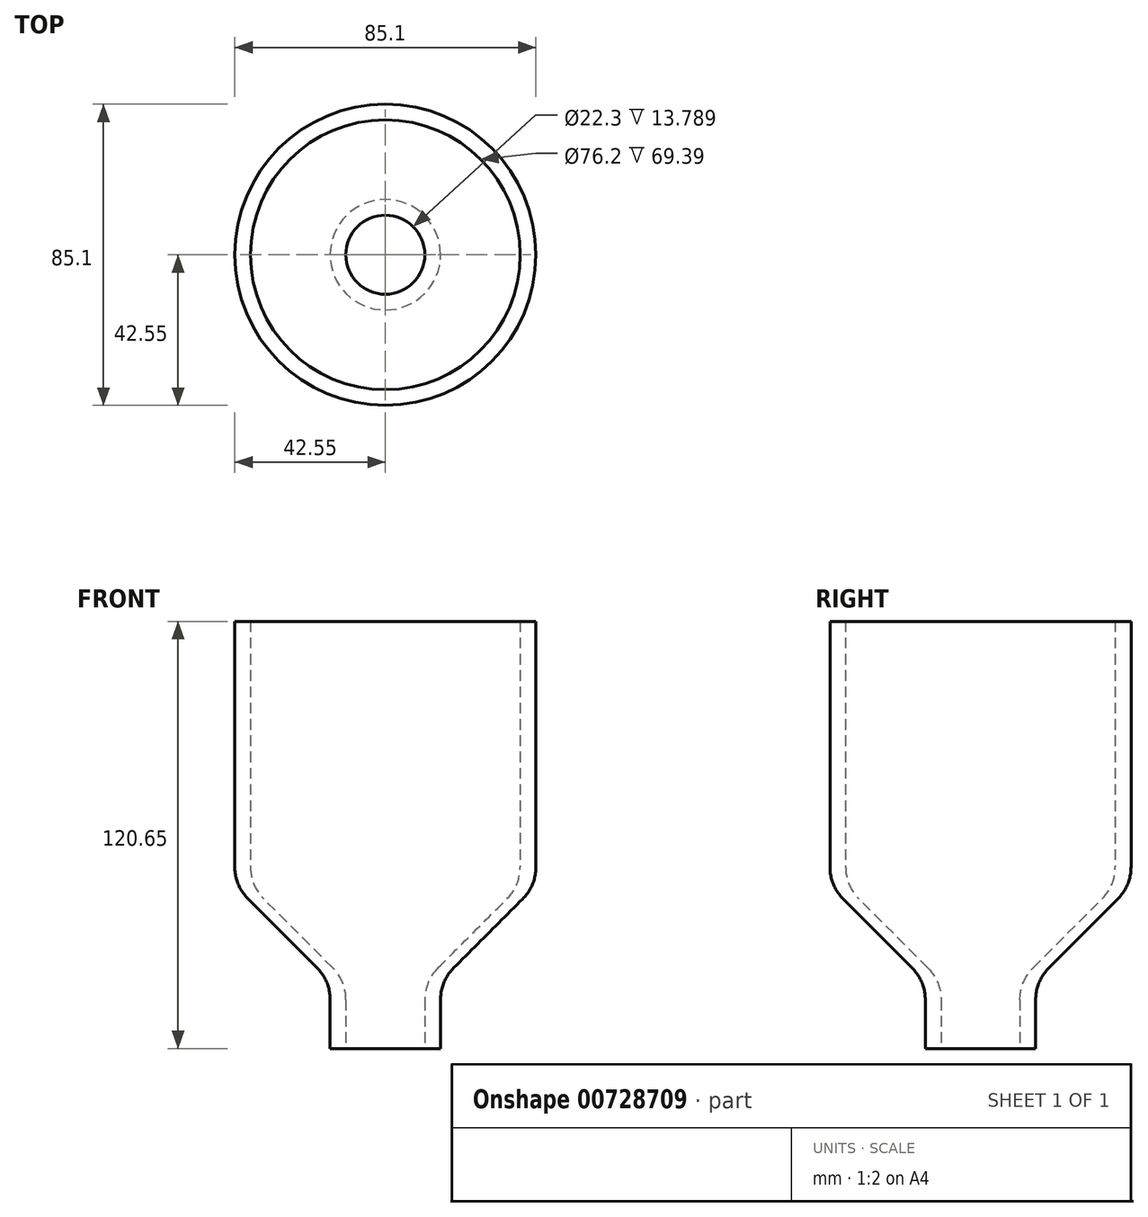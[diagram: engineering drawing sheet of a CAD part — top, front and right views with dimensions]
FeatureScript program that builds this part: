
annotation { "Feature Type Name" : "Feature", "Feature Type Description" : "" }
export const myFeature = defineFeature(function(context is Context, id is Id, definition is map)
    precondition{}
    {
        {
            var Q0;
            Q0=qCreatedBy(makeId("Front.planeOp"),FACE);
            var sketch = newSketch(context, id + "F0", { "sketchPlane" : qUnion([Q0])});
            skLineSegment(sketch, "E0", {"start": v(-38.1, 101.6) * mm, "end": v(-38.1, 26.95) * mm});
            skLineSegment(sketch, "E1", {"start": v(-38.1, 26.95) * mm, "end": v(-11.15, 0) * mm});
            skLineSegment(sketch, "E2", {"start": v(-15.6, 0) * mm, "end": v(-42.55, 26.95) * mm});
            skLineSegment(sketch, "E3", {"start": v(-42.55, 26.95) * mm, "end": v(-42.55, 101.6) * mm});
            skLineSegment(sketch, "E4", {"start": v(-42.55, 101.6) * mm, "end": v(-38.1, 101.6) * mm});
            skLineSegment(sketch, "E5", {"start": v(-11.15, 0) * mm, "end": v(-11.15, -19.05) * mm});
            skLineSegment(sketch, "E6", {"start": v(-11.15, -19.05) * mm, "end": v(-15.6, -19.05) * mm});
            skLineSegment(sketch, "E7", {"start": v(-15.6, -19.05) * mm, "end": v(-15.6, 0) * mm});
            skLineSegment(sketch, "E8", {"start": v(0, 0) * mm, "end": v(0, 44.65) * mm, "construction": true});
            skSolve(sketch);
        }
        {
            var Q0;
            Q0 = qSketchRegion(id + "F0", true);
            var Q1;
            Q1=sQuery(id+"F0.wireOp",EDGE,"E8");
            revolve(context, id + "F1", {"surfaceOperationType" : NewSurfaceOperationType.NEW, "entities" : qUnion([Q0]), "axis" : qUnion([Q1]), "revolveType" : RevolveType.FULL});
        }
        {
            var Q0;
            Q0=makeQuery(id+"F1.opRevolve","SWEPT_EDGE",EDGE,{"disambiguationData":[OSD([sQuery(id+"F0.wireOp",EDGE,"E2"),sQuery(id+"F0.wireOp",EDGE,"E3")])]});
            var Q1;
            Q1=makeQuery(id+"F1.opRevolve","SWEPT_EDGE",EDGE,{"disambiguationData":[OSD([sQuery(id+"F0.wireOp",EDGE,"E2"),sQuery(id+"F0.wireOp",EDGE,"E7")])]});
            var Q2;
            Q2=makeQuery(id+"F1.opRevolve","SWEPT_EDGE",EDGE,{"disambiguationData":[OSD([sQuery(id+"F0.wireOp",EDGE,"E0"),sQuery(id+"F0.wireOp",EDGE,"E1")])]});
            var Q3;
            Q3=makeQuery(id+"F1.opRevolve","SWEPT_EDGE",EDGE,{"disambiguationData":[OSD([sQuery(id+"F0.wireOp",EDGE,"E1"),sQuery(id+"F0.wireOp",EDGE,"E5")])]});
            fillet(context, id + "F2", {"entities" : qUnion([Q0, Q1, Q2, Q3]), "radius" : 12.7 * mm, "tangentPropagation" : true, "allowEdgeOverflow" : false});
        }
    });
